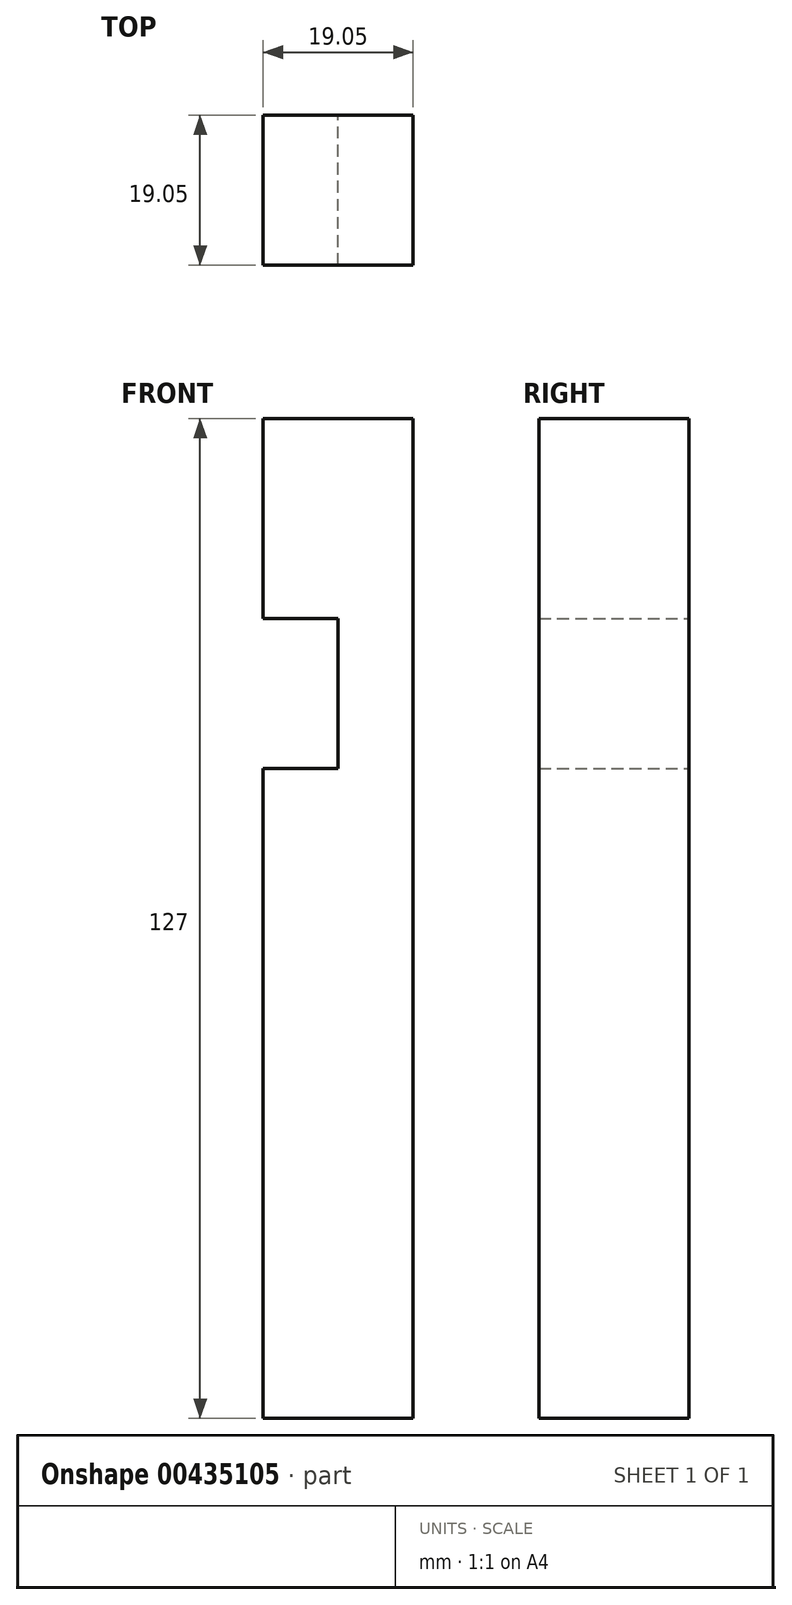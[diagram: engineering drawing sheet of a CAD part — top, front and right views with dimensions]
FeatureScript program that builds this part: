
annotation { "Feature Type Name" : "Feature", "Feature Type Description" : "" }
export const myFeature = defineFeature(function(context is Context, id is Id, definition is map)
    precondition{}
    {
        {
            var Q0;
            Q0=qCreatedBy(makeId("Front.planeOp"),FACE);
            var sketch = newSketch(context, id + "F0", { "sketchPlane" : qUnion([Q0])});
            skLineSegment(sketch, "E0", {"start": v(29.01, -52.98) * mm, "end": v(29.01, 74.02) * mm});
            skLineSegment(sketch, "E1", {"start": v(29.01, -52.98) * mm, "end": v(9.96, -52.98) * mm});
            skLineSegment(sketch, "E2", {"start": v(29.01, 74.02) * mm, "end": v(9.96, 74.02) * mm});
            skLineSegment(sketch, "E3", {"start": v(9.96, 74.02) * mm, "end": v(9.96, 48.62) * mm});
            skLineSegment(sketch, "E4", {"start": v(9.96, 48.62) * mm, "end": v(19.49, 48.62) * mm});
            skLineSegment(sketch, "E5", {"start": v(19.49, 48.62) * mm, "end": v(19.49, 29.57) * mm});
            skLineSegment(sketch, "E6", {"start": v(19.49, 29.57) * mm, "end": v(9.96, 29.57) * mm});
            skLineSegment(sketch, "E7", {"start": v(9.96, 29.57) * mm, "end": v(9.96, -52.98) * mm});
            skSolve(sketch);
        }
        {
            var Q0;
            Q0 = qSketchRegion(id + "F0", true);
            extrude(context, id + "F1", {"entities" : qUnion([Q0]), "depth" : 19.05 * mm});
        }
    });
